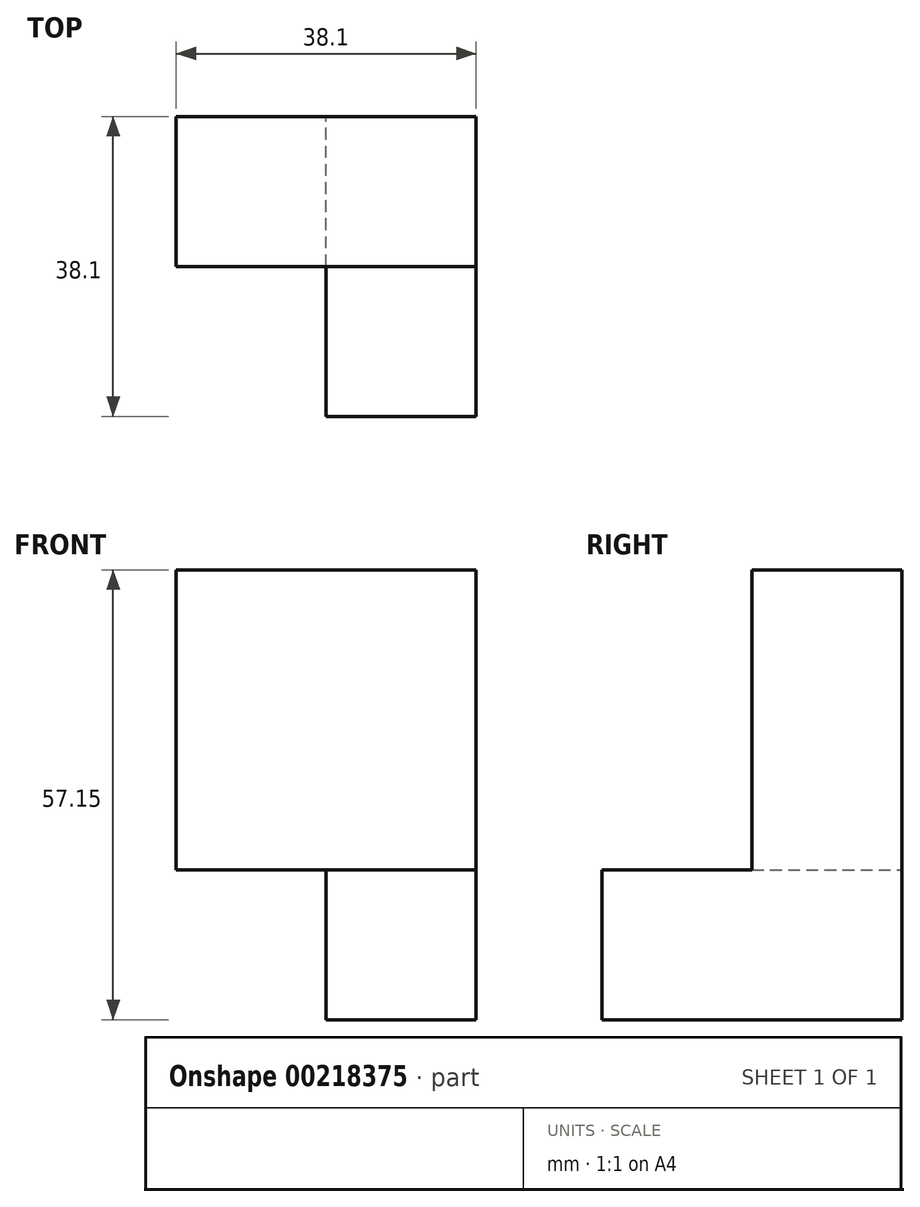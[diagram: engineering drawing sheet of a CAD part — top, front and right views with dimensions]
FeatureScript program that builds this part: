
annotation { "Feature Type Name" : "Feature", "Feature Type Description" : "" }
export const myFeature = defineFeature(function(context is Context, id is Id, definition is map)
    precondition{}
    {
        {
            var Q0;
            Q0=qCreatedBy(makeId("Front.planeOp"),FACE);
            var sketch = newSketch(context, id + "F0", { "sketchPlane" : qUnion([Q0])});
            skLineSegment(sketch, "E0.bottom", {"start": v(-27.22, -4.31) * mm, "end": v(-65.32, -4.31) * mm});
            skLineSegment(sketch, "E0.top", {"start": v(-27.22, 33.79) * mm, "end": v(-65.32, 33.79) * mm});
            skLineSegment(sketch, "E0.left", {"start": v(-27.22, -4.31) * mm, "end": v(-27.22, 33.79) * mm});
            skLineSegment(sketch, "E0.right", {"start": v(-65.32, -4.31) * mm, "end": v(-65.32, 33.79) * mm});
            skPoint(sketch, "E0.middle", {"position": v(-46.27, 14.74) * mm});
            skLineSegment(sketch, "E1", {"start": v(-27.22, -4.31) * mm, "end": v(-27.22, -23.36) * mm});
            skLineSegment(sketch, "E2", {"start": v(-46.27, -23.36) * mm, "end": v(-27.22, -23.36) * mm});
            skLineSegment(sketch, "E3", {"start": v(-46.27, -23.36) * mm, "end": v(-46.27, -4.31) * mm});
            skSolve(sketch);
        }
        {
            var Q0;
            Q0=makeQuery(id+"F0.imprint","IMPRINT",FACE,{"disambiguationData":[TD([[makeQuery(id+"F0.imprint","IMPRINT",EDGE,{"derivedFrom":sQuery(id+"F0.wireOp",EDGE,"E0.top")}),1.0]])]});
            extrude(context, id + "F1", {"entities" : qUnion([Q0]), "depth" : 19.05 * mm});
        }
        {
            var Q0;
            {var subQ0=sQuery(id+"F0.wireOp",EDGE,"E1");Q0=makeQuery(id+"F0.imprint","IMPRINT",FACE,{"disambiguationData":[TD([[makeQuery(id+"F0.imprint","IMPRINT",EDGE,{"derivedFrom":subQ0}),-1.0]])]});}
            extrude(context, id + "F2", {"entities" : qUnion([Q0]), "operationType" : NewBodyOperationType.ADD, "depth" : 38.1 * mm});
        }
    });
